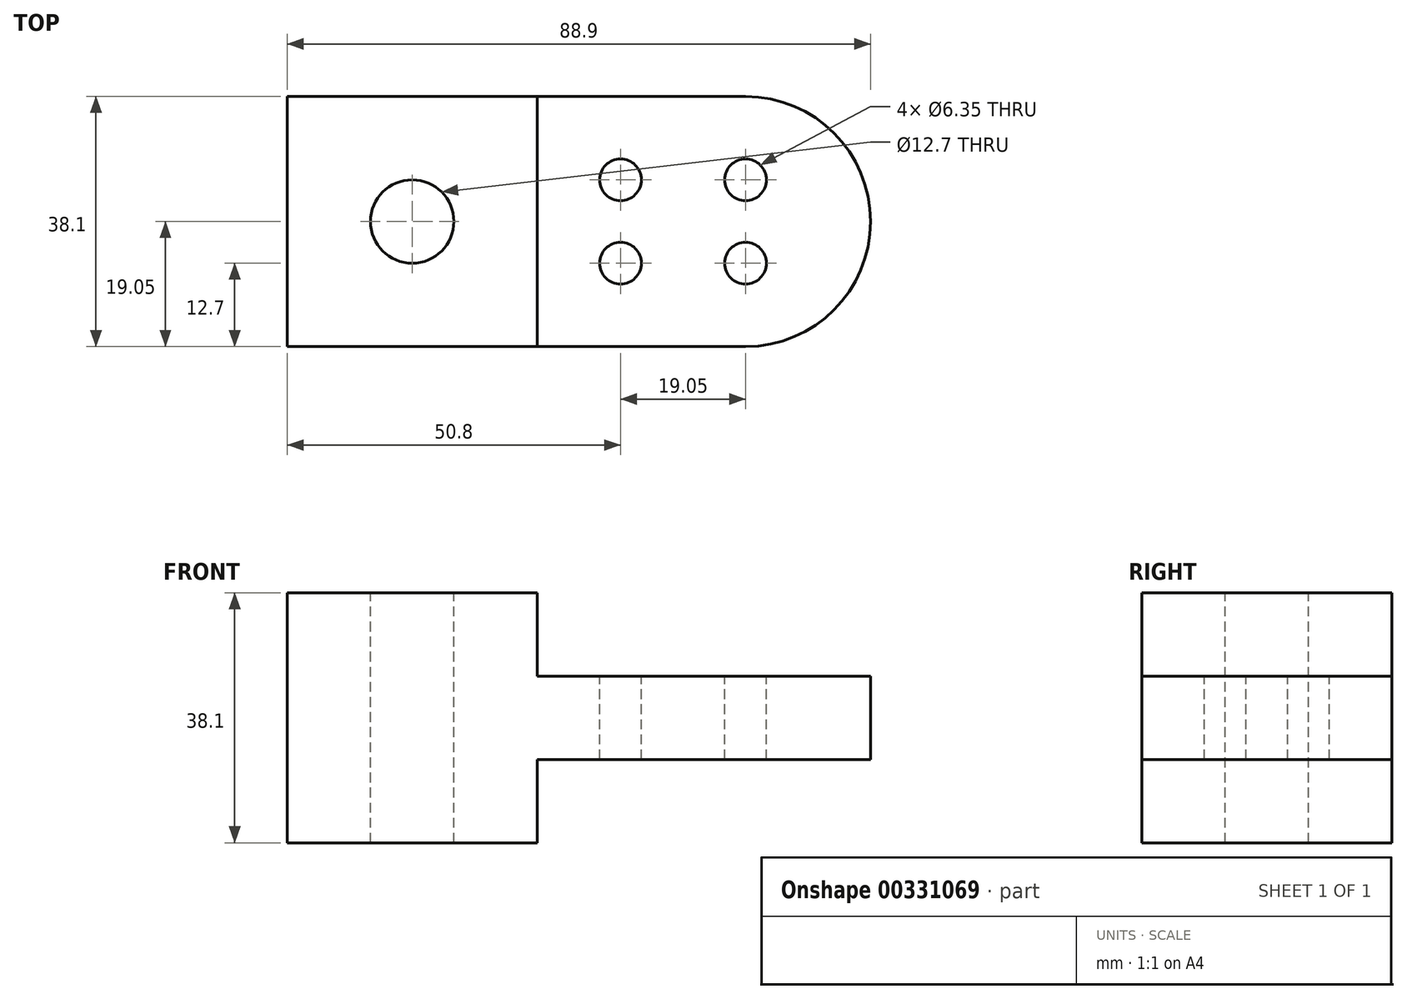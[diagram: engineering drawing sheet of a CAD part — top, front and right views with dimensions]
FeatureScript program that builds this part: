
annotation { "Feature Type Name" : "Feature", "Feature Type Description" : "" }
export const myFeature = defineFeature(function(context is Context, id is Id, definition is map)
    precondition{}
    {
        {
            var Q0;
            Q0=qCreatedBy(makeId("Top.planeOp"),FACE);
            var sketch = newSketch(context, id + "F0", { "sketchPlane" : qUnion([Q0])});
            skLineSegment(sketch, "E0", {"start": v(0, 0) * mm, "end": v(0, 38.1) * mm});
            skLineSegment(sketch, "E1", {"start": v(0, 38.1) * mm, "end": v(38.1, 38.1) * mm});
            skLineSegment(sketch, "E2", {"start": v(38.1, 38.1) * mm, "end": v(38.1, 0) * mm});
            skLineSegment(sketch, "E3", {"start": v(38.1, 0) * mm, "end": v(0, 0) * mm});
            skLineSegment(sketch, "E4", {"start": v(38.1, 38.1) * mm, "end": v(69.85, 38.1) * mm});
            skLineSegment(sketch, "E5", {"start": v(38.1, 0) * mm, "end": v(69.85, 0) * mm});
            skArc(sketch, "E6", {"start": v(69.85, 0) * mm, "mid": v(88.9, 19.05) * mm, "end": v(69.85, 38.1) * mm});
            skSolve(sketch);
        }
        {
            var Q0;
            Q0 = qSketchRegion(id + "F0", true);
            extrude(context, id + "F1", {"entities" : qUnion([Q0]), "depth" : 38.1 * mm});
        }
        {
            var Q0;
            Q0=makeQuery(id+"F1.opExtrude","SWEPT_FACE",FACE,{"disambiguationData":[OSD([sQuery(id+"F0.wireOp",EDGE,"E3"),sQuery(id+"F0.wireOp",EDGE,"E5")])]});
            var sketch = newSketch(context, id + "F2", { "sketchPlane" : qUnion([Q0])});
            skLineSegment(sketch, "E7", {"start": v(0, 38.1) * mm, "end": v(38.1, 38.1) * mm});
            skLineSegment(sketch, "E8", {"start": v(38.1, 38.1) * mm, "end": v(38.1, 25.4) * mm});
            skLineSegment(sketch, "E9", {"start": v(38.1, 12.7) * mm, "end": v(38.1, 0) * mm});
            skLineSegment(sketch, "E10", {"start": v(38.1, 0) * mm, "end": v(0, 0) * mm});
            skLineSegment(sketch, "E11", {"start": v(0, 0) * mm, "end": v(0, 38.1) * mm});
            skLineSegment(sketch, "E12", {"start": v(38.1, 25.4) * mm, "end": v(88.9, 25.4) * mm});
            skLineSegment(sketch, "E13", {"start": v(88.9, 25.4) * mm, "end": v(88.9, 12.7) * mm});
            skLineSegment(sketch, "E14", {"start": v(88.9, 12.7) * mm, "end": v(38.1, 12.7) * mm});
            skLineSegment(sketch, "E15", {"start": v(88.9, 12.7) * mm, "end": v(88.9, 0) * mm});
            skLineSegment(sketch, "E16", {"start": v(88.9, 0) * mm, "end": v(69.85, 0) * mm});
            skLineSegment(sketch, "E17", {"start": v(69.85, 0) * mm, "end": v(69.85, 12.7) * mm});
            skLineSegment(sketch, "E18", {"start": v(69.85, 12.7) * mm, "end": v(88.9, 12.7) * mm});
            skLineSegment(sketch, "E19", {"start": v(88.9, 25.4) * mm, "end": v(88.9, 38.1) * mm});
            skLineSegment(sketch, "E20", {"start": v(88.9, 38.1) * mm, "end": v(69.85, 38.1) * mm});
            skLineSegment(sketch, "E21", {"start": v(69.85, 38.1) * mm, "end": v(69.85, 25.4) * mm});
            skLineSegment(sketch, "E22", {"start": v(69.85, 25.4) * mm, "end": v(88.9, 25.4) * mm});
            skSolve(sketch);
        }
        {
            var Q0;
            {var subQ0=sQuery(id+"F2.wireOp",EDGE,"E8");Q0=makeQuery(id+"F2.imprint","IMPRINT",FACE,{"disambiguationData":[TD([[makeQuery(id+"F2.imprint","IMPRINT",EDGE,{"derivedFrom":subQ0}),1.0]])]});}
            var Q1;
            Q1=makeQuery(id+"F2.imprint","IMPRINT",FACE,{"disambiguationData":[TD([[makeQuery(id+"F2.imprint","IMPRINT",EDGE,{"derivedFrom":sQuery(id+"F2.wireOp",EDGE,"E19")}),1.0]])]});
            var Q2;
            {var subQ0=sQuery(id+"F2.wireOp",EDGE,"E9");Q2=makeQuery(id+"F2.imprint","IMPRINT",FACE,{"disambiguationData":[TD([[makeQuery(id+"F2.imprint","IMPRINT",EDGE,{"derivedFrom":subQ0}),1.0]])]});}
            var Q3;
            Q3=makeQuery(id+"F2.imprint","IMPRINT",FACE,{"disambiguationData":[TD([[makeQuery(id+"F2.imprint","IMPRINT",EDGE,{"derivedFrom":sQuery(id+"F2.wireOp",EDGE,"E15")}),-1.0]])]});
            extrude(context, id + "F3", {"entities" : qUnion([Q0, Q1, Q2, Q3]), "operationType" : NewBodyOperationType.REMOVE, "endBound" : BoundingType.THROUGH_ALL, "oppositeDirection" : true, "depth" : 25.4 * mm});
        }
        {
            var Q0;
            Q0=makeQuery(id+"F1.opExtrude","CAP_FACE",FACE,{"disambiguationData":[OSD([sQuery(id+"F0.wireOp",EDGE,"E0"),sQuery(id+"F0.wireOp",EDGE,"E1"),sQuery(id+"F0.wireOp",EDGE,"E3"),sQuery(id+"F0.wireOp",EDGE,"E4"),sQuery(id+"F0.wireOp",EDGE,"E5"),sQuery(id+"F0.wireOp",EDGE,"E6")])],"isStart":false});
            var sketch = newSketch(context, id + "F4", { "sketchPlane" : qUnion([Q0])});
            skCircle(sketch, "E23", {"center": v(19.05, 19.05) * mm, "radius": 6.35 * mm});
            skCircle(sketch, "E24", {"center": v(50.8, 25.4) * mm, "radius": 3.18 * mm});
            skCircle(sketch, "E25", {"center": v(69.85, 25.4) * mm, "radius": 3.18 * mm});
            skCircle(sketch, "E26", {"center": v(50.8, 12.7) * mm, "radius": 3.18 * mm});
            skCircle(sketch, "E27", {"center": v(69.85, 12.7) * mm, "radius": 3.18 * mm});
            skSolve(sketch);
        }
        {
            var Q0;
            Q0=makeQuery(id+"F4.imprint","IMPRINT",FACE,{"disambiguationData":[TD([[makeQuery(id+"F4.imprint","IMPRINT",EDGE,{"derivedFrom":sQuery(id+"F4.wireOp",EDGE,"E23")}),1.0]])]});
            var Q1;
            Q1=makeQuery(id+"F4.imprint","IMPRINT",FACE,{"disambiguationData":[TD([[makeQuery(id+"F4.imprint","IMPRINT",EDGE,{"derivedFrom":sQuery(id+"F4.wireOp",EDGE,"E24")}),1.0]])]});
            var Q2;
            Q2=makeQuery(id+"F4.imprint","IMPRINT",FACE,{"disambiguationData":[TD([[makeQuery(id+"F4.imprint","IMPRINT",EDGE,{"derivedFrom":sQuery(id+"F4.wireOp",EDGE,"E25")}),1.0]])]});
            var Q3;
            Q3=makeQuery(id+"F4.imprint","IMPRINT",FACE,{"disambiguationData":[TD([[makeQuery(id+"F4.imprint","IMPRINT",EDGE,{"derivedFrom":sQuery(id+"F4.wireOp",EDGE,"E26")}),1.0]])]});
            var Q4;
            Q4=makeQuery(id+"F4.imprint","IMPRINT",FACE,{"disambiguationData":[TD([[makeQuery(id+"F4.imprint","IMPRINT",EDGE,{"derivedFrom":sQuery(id+"F4.wireOp",EDGE,"E27")}),1.0]])]});
            var Q5;
            Q5=sQuery(id+"F4.wireOp",EDGE,"E24");
            var Q6;
            Q6=sQuery(id+"F4.wireOp",EDGE,"E25");
            var Q7;
            Q7=sQuery(id+"F4.wireOp",EDGE,"E27");
            var Q8;
            Q8=sQuery(id+"F4.wireOp",EDGE,"E26");
            var Q9;
            Q9=sQuery(id+"F4.wireOp",EDGE,"E23");
            extrude(context, id + "F5", {"entities" : qUnion([Q0, Q1, Q2, Q3, Q4]), "operationType" : NewBodyOperationType.REMOVE, "surfaceEntities" : qUnion([Q5, Q6, Q7, Q8, Q9]), "endBound" : BoundingType.THROUGH_ALL, "oppositeDirection" : true, "depth" : 25.4 * mm});
        }
    });
